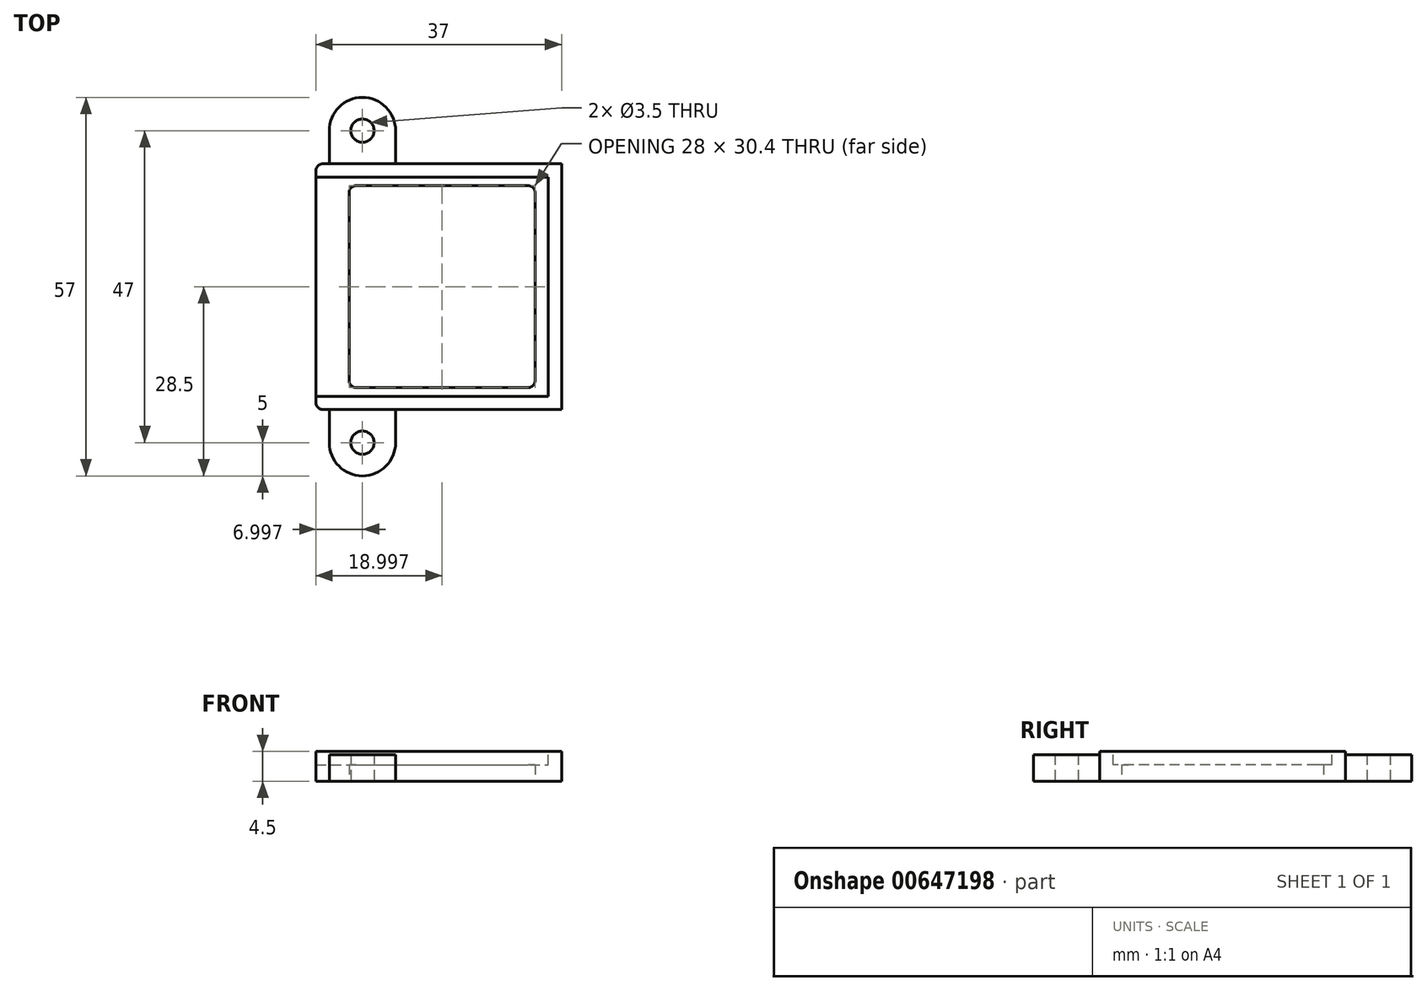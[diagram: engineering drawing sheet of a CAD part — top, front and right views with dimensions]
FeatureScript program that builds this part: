
annotation { "Feature Type Name" : "Feature", "Feature Type Description" : "" }
export const myFeature = defineFeature(function(context is Context, id is Id, definition is map)
    precondition{}
    {
        {
            var Q0;
            Q0=qCreatedBy(makeId("Top.planeOp"),FACE);
            var sketch = newSketch(context, id + "F0", { "sketchPlane" : qUnion([Q0])});
            skLineSegment(sketch, "E0.bottom", {"start": v(-25.96, 17.81) * mm, "end": v(11.04, 17.81) * mm});
            skLineSegment(sketch, "E0.top", {"start": v(-25.96, -19.19) * mm, "end": v(11.04, -19.19) * mm});
            skLineSegment(sketch, "E0.left", {"start": v(-25.96, 17.81) * mm, "end": v(-25.96, -19.19) * mm});
            skLineSegment(sketch, "E0.right", {"start": v(11.04, 17.81) * mm, "end": v(11.04, -19.19) * mm});
            skLineSegment(sketch, "E1.bottom", {"start": v(-20.96, 14.51) * mm, "end": v(7.04, 14.51) * mm});
            skLineSegment(sketch, "E1.top", {"start": v(-20.96, -15.89) * mm, "end": v(7.04, -15.89) * mm});
            skLineSegment(sketch, "E1.left", {"start": v(-20.96, 14.51) * mm, "end": v(-20.96, -15.89) * mm});
            skLineSegment(sketch, "E1.right", {"start": v(7.04, 14.51) * mm, "end": v(7.04, -15.89) * mm});
            skSolve(sketch);
        }
        {
            var Q0;
            Q0 = qSketchRegion(id + "F0", true);
            extrude(context, id + "F1", {"entities" : qUnion([Q0]), "depth" : 4.5 * mm, "offsetDistance" : 25 * mm});
        }
        {
            var Q0;
            Q0=makeQuery(id+"F1.opExtrude","CAP_FACE",FACE,{"disambiguationData":[OSD([sQuery(id+"F0.wireOp",EDGE,"E0.bottom"),sQuery(id+"F0.wireOp",EDGE,"E0.top"),sQuery(id+"F0.wireOp",EDGE,"E0.left"),sQuery(id+"F0.wireOp",EDGE,"E0.right"),sQuery(id+"F0.wireOp",EDGE,"E1.bottom"),sQuery(id+"F0.wireOp",EDGE,"E1.top"),sQuery(id+"F0.wireOp",EDGE,"E1.left"),sQuery(id+"F0.wireOp",EDGE,"E1.right")])],"isStart":false});
            var sketch = newSketch(context, id + "F2", { "sketchPlane" : qUnion([Q0])});
            skLineSegment(sketch, "E2.bottom", {"start": v(-25.96, 15.81) * mm, "end": v(9.04, 15.81) * mm});
            skLineSegment(sketch, "E2.top", {"start": v(-25.96, -17.19) * mm, "end": v(9.04, -17.19) * mm});
            skLineSegment(sketch, "E2.left", {"start": v(-25.96, 15.81) * mm, "end": v(-25.96, -17.19) * mm});
            skLineSegment(sketch, "E2.right", {"start": v(9.04, 15.81) * mm, "end": v(9.04, -17.19) * mm});
            skSolve(sketch);
        }
        {
            var Q0;
            Q0 = qSketchRegion(id + "F2", true);
            extrude(context, id + "F3", {"entities" : qUnion([Q0]), "operationType" : NewBodyOperationType.REMOVE, "oppositeDirection" : true, "depth" : 2 * mm, "offsetDistance" : 25 * mm});
        }
        {
            var Q0;
            Q0=qCreatedBy(makeId("Top.planeOp"),FACE);
            var sketch = newSketch(context, id + "F4", { "sketchPlane" : qUnion([Q0])});
            skArc(sketch, "E3", {"start": v(-13.96, 22.81) * mm, "mid": v(-18.96, 27.81) * mm, "end": v(-23.96, 22.81) * mm});
            skLineSegment(sketch, "E4.bottom", {"start": v(-23.96, 17.81) * mm, "end": v(-13.96, 17.81) * mm});
            skLineSegment(sketch, "E4.left", {"start": v(-23.96, 17.81) * mm, "end": v(-23.96, 22.81) * mm});
            skLineSegment(sketch, "E4.right", {"start": v(-13.96, 17.81) * mm, "end": v(-13.96, 22.81) * mm});
            skPoint(sketch, "E5.orphan", {"position": v(-23.96, 27.81) * mm});
            skPoint(sketch, "E6.orphan", {"position": v(-13.96, 27.81) * mm});
            skCircle(sketch, "E7", {"center": v(-18.96, 22.81) * mm, "radius": 1.75 * mm});
            skArc(sketch, "E8", {"start": v(-23.96, -24.19) * mm, "mid": v(-18.96, -29.19) * mm, "end": v(-13.96, -24.19) * mm});
            skLineSegment(sketch, "E9.bottom", {"start": v(-13.96, -19.19) * mm, "end": v(-23.96, -19.19) * mm});
            skLineSegment(sketch, "E9.left", {"start": v(-13.96, -19.19) * mm, "end": v(-13.96, -24.19) * mm});
            skLineSegment(sketch, "E9.right", {"start": v(-23.96, -19.19) * mm, "end": v(-23.96, -24.19) * mm});
            skPoint(sketch, "E10.orphan", {"position": v(-23.96, -29.19) * mm});
            skPoint(sketch, "E11.orphan", {"position": v(-13.96, -29.19) * mm});
            skCircle(sketch, "E12", {"center": v(-18.96, -24.19) * mm, "radius": 1.75 * mm});
            skSolve(sketch);
        }
        {
            var Q0;
            Q0 = qSketchRegion(id + "F4", true);
            extrude(context, id + "F5", {"entities" : qUnion([Q0]), "operationType" : NewBodyOperationType.ADD, "depth" : 4 * mm, "offsetDistance" : 25 * mm});
        }
        {
            var Q0;
            Q0 = qSketchRegion(id + "F4", true);
            extrude(context, id + "F6", {"entities" : qUnion([Q0]), "operationType" : NewBodyOperationType.ADD, "depth" : 4 * mm, "offsetDistance" : 25 * mm});
        }
        {
            var Q0;
            Q0=makeQuery(id+"F1.opExtrude","SWEPT_EDGE",EDGE,{"disambiguationData":[OSD([sQuery(id+"F0.wireOp",EDGE,"E1.bottom"),sQuery(id+"F0.wireOp",EDGE,"E1.right")])]});
            var Q1;
            Q1=makeQuery(id+"F1.opExtrude","SWEPT_EDGE",EDGE,{"disambiguationData":[OSD([sQuery(id+"F0.wireOp",EDGE,"E1.bottom"),sQuery(id+"F0.wireOp",EDGE,"E1.left")])]});
            var Q2;
            Q2=makeQuery(id+"F1.opExtrude","SWEPT_EDGE",EDGE,{"disambiguationData":[OSD([sQuery(id+"F0.wireOp",EDGE,"E1.top"),sQuery(id+"F0.wireOp",EDGE,"E1.left")])]});
            var Q3;
            Q3=makeQuery(id+"F1.opExtrude","SWEPT_EDGE",EDGE,{"disambiguationData":[OSD([sQuery(id+"F0.wireOp",EDGE,"E1.top"),sQuery(id+"F0.wireOp",EDGE,"E1.right")])]});
            var Q4;
            Q4=makeQuery(id+"F1.opExtrude","SWEPT_EDGE",EDGE,{"disambiguationData":[OSD([sQuery(id+"F0.wireOp",EDGE,"E0.top"),sQuery(id+"F0.wireOp",EDGE,"E0.left")])]});
            var Q5;
            Q5=makeQuery(id+"F1.opExtrude","SWEPT_EDGE",EDGE,{"disambiguationData":[OSD([sQuery(id+"F0.wireOp",EDGE,"E0.bottom"),sQuery(id+"F0.wireOp",EDGE,"E0.left")])]});
            fillet(context, id + "F7", {"entities" : qUnion([Q0, Q1, Q2, Q3, Q4, Q5]), "radius" : 1 * mm, "tangentPropagation" : true, "allowEdgeOverflow" : false});
        }
    });
